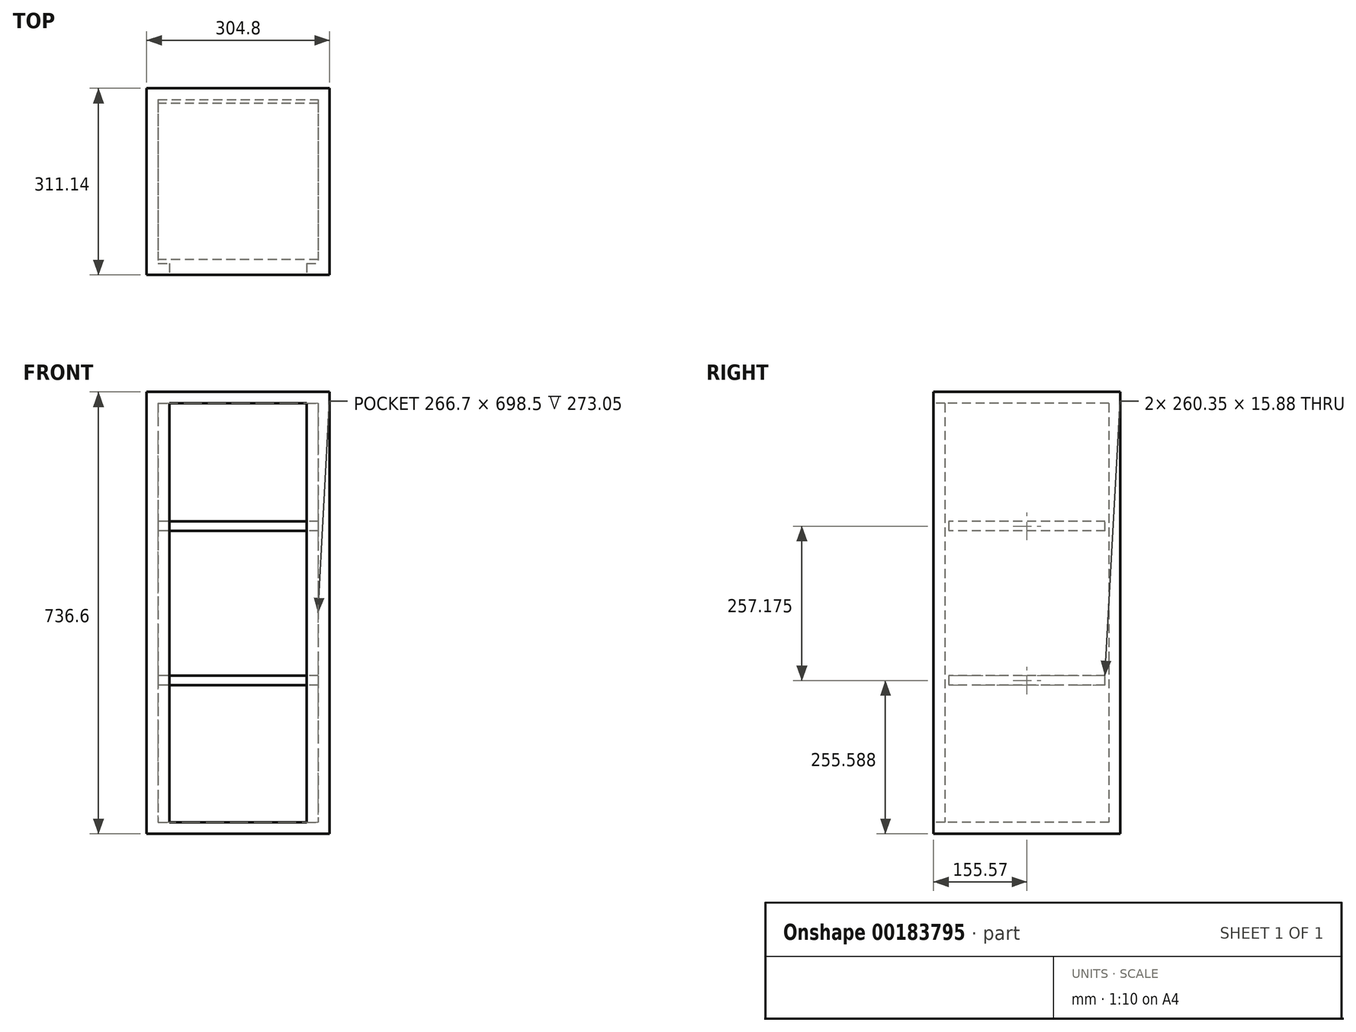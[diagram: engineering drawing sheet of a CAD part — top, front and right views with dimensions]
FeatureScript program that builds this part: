
annotation { "Feature Type Name" : "Feature", "Feature Type Description" : "" }
export const myFeature = defineFeature(function(context is Context, id is Id, definition is map)
    precondition{}
    {
        {
            var Q0;
            Q0=qCreatedBy(makeId("Top.planeOp"),FACE);
            var sketch = newSketch(context, id + "F0", { "sketchPlane" : qUnion([Q0])});
            skLineSegment(sketch, "E0.bottom", {"start": v(-133.35, 136.53) * mm, "end": v(133.35, 136.53) * mm});
            skLineSegment(sketch, "E0.top", {"start": v(-133.35, -136.53) * mm, "end": v(-114.3, -136.53) * mm});
            skLineSegment(sketch, "E0.left", {"start": v(-133.35, 136.52) * mm, "end": v(-133.35, -136.53) * mm});
            skLineSegment(sketch, "E0.right", {"start": v(133.35, 136.52) * mm, "end": v(133.35, -136.52) * mm});
            skLineSegment(sketch, "E1", {"start": v(133.35, 0) * mm, "end": v(-133.35, 0) * mm, "construction": true});
            skLineSegment(sketch, "E2", {"start": v(0, 136.53) * mm, "end": v(0, -136.53) * mm, "construction": true});
            skLineSegment(sketch, "E3.0", {"start": v(-152.4, 155.57) * mm, "end": v(152.4, 155.57) * mm});
            skLineSegment(sketch, "E3.1", {"start": v(-152.4, 155.57) * mm, "end": v(-152.4, -155.57) * mm});
            skLineSegment(sketch, "E3.2", {"start": v(-152.4, -155.57) * mm, "end": v(-114.3, -155.57) * mm});
            skLineSegment(sketch, "E3.3", {"start": v(152.4, 155.57) * mm, "end": v(152.4, -155.57) * mm});
            skLineSegment(sketch, "E4", {"start": v(114.3, -136.53) * mm, "end": v(114.3, -155.57) * mm});
            skLineSegment(sketch, "E5", {"start": v(-114.3, -136.53) * mm, "end": v(-114.3, -155.58) * mm});
            skLineSegment(sketch, "E6", {"start": v(-114.3, -136.53) * mm, "end": v(114.3, -136.53) * mm, "construction": true});
            skLineSegment(sketch, "E7", {"start": v(114.3, -136.53) * mm, "end": v(133.35, -136.53) * mm});
            skLineSegment(sketch, "E8", {"start": v(114.3, -155.57) * mm, "end": v(152.4, -155.57) * mm});
            skLineSegment(sketch, "E9", {"start": v(-114.3, -155.57) * mm, "end": v(114.3, -155.57) * mm, "construction": true});
            skSolve(sketch);
        }
        {
            var Q0;
            Q0=makeQuery(id+"F0.imprint","IMPRINT",FACE,{"disambiguationData":[TD([[makeQuery(id+"F0.imprint","IMPRINT",EDGE,{"derivedFrom":sQuery(id+"F0.wireOp",EDGE,"E0.bottom")}),1.0]])]});
            extrude(context, id + "F1", {"entities" : qUnion([Q0]), "depth" : 698.5 * mm});
        }
        {
            var Q0;
            Q0=makeQuery(id+"F1.opExtrude","CAP_FACE",FACE,{"disambiguationData":[OSD([sQuery(id+"F0.wireOp",EDGE,"E0.bottom"),sQuery(id+"F0.wireOp",EDGE,"E0.top"),sQuery(id+"F0.wireOp",EDGE,"E0.left"),sQuery(id+"F0.wireOp",EDGE,"E0.right"),sQuery(id+"F0.wireOp",EDGE,"E3.0"),sQuery(id+"F0.wireOp",EDGE,"E3.1"),sQuery(id+"F0.wireOp",EDGE,"E3.2"),sQuery(id+"F0.wireOp",EDGE,"E3.3"),sQuery(id+"F0.wireOp",EDGE,"E4"),sQuery(id+"F0.wireOp",EDGE,"E5"),sQuery(id+"F0.wireOp",EDGE,"E7"),sQuery(id+"F0.wireOp",EDGE,"E8")])],"isStart":false});
            var sketch = newSketch(context, id + "F2", { "sketchPlane" : qUnion([Q0])});
            skLineSegment(sketch, "E10.bottom", {"start": v(-152.4, 155.57) * mm, "end": v(152.4, 155.57) * mm});
            skLineSegment(sketch, "E10.top", {"start": v(-152.4, -155.57) * mm, "end": v(152.4, -155.57) * mm});
            skLineSegment(sketch, "E10.left", {"start": v(-152.4, 155.57) * mm, "end": v(-152.4, -155.57) * mm});
            skLineSegment(sketch, "E10.right", {"start": v(152.4, 155.57) * mm, "end": v(152.4, -155.57) * mm});
            skSolve(sketch);
        }
        {
            var Q0;
            Q0=makeQuery(id+"F2.imprint","IMPRINT",FACE,{"disambiguationData":[TD([[makeQuery(id+"F2.imprint","IMPRINT",EDGE,{"derivedFrom":sQuery(id+"F2.wireOp",EDGE,"E10.bottom")}),-1.0]])]});
            var Q1;
            Q1=makeQuery(id+"F2.imprint","IMPRINT",FACE,{"disambiguationData":[TD([[makeQuery(id+"F2.imprint","IMPRINT",EDGE,{"derivedFrom":makeQuery(id+"F1.opExtrude","CAP_EDGE",EDGE,{"disambiguationData":[OSD([sQuery(id+"F0.wireOp",EDGE,"E0.bottom")])],"isStart":false})}),-1.0]])]});
            extrude(context, id + "F3", {"entities" : qUnion([Q0, Q1]), "operationType" : NewBodyOperationType.ADD, "depth" : 19.05 * mm});
        }
        {
            var Q0;
            Q0=makeQuery(id+"F1.opExtrude","CAP_FACE",FACE,{"disambiguationData":[OSD([sQuery(id+"F0.wireOp",EDGE,"E0.bottom"),sQuery(id+"F0.wireOp",EDGE,"E0.top"),sQuery(id+"F0.wireOp",EDGE,"E0.left"),sQuery(id+"F0.wireOp",EDGE,"E0.right"),sQuery(id+"F0.wireOp",EDGE,"E3.0"),sQuery(id+"F0.wireOp",EDGE,"E3.1"),sQuery(id+"F0.wireOp",EDGE,"E3.2"),sQuery(id+"F0.wireOp",EDGE,"E3.3"),sQuery(id+"F0.wireOp",EDGE,"E4"),sQuery(id+"F0.wireOp",EDGE,"E5"),sQuery(id+"F0.wireOp",EDGE,"E7"),sQuery(id+"F0.wireOp",EDGE,"E8")])],"isStart":true});
            var sketch = newSketch(context, id + "F4", { "sketchPlane" : qUnion([Q0])});
            skLineSegment(sketch, "E11.bottom", {"start": v(-152.4, -155.57) * mm, "end": v(152.4, -155.57) * mm});
            skLineSegment(sketch, "E11.top", {"start": v(-152.4, 155.57) * mm, "end": v(152.4, 155.57) * mm});
            skLineSegment(sketch, "E11.left", {"start": v(-152.4, -155.57) * mm, "end": v(-152.4, 155.57) * mm});
            skLineSegment(sketch, "E11.right", {"start": v(152.4, -155.57) * mm, "end": v(152.4, 155.57) * mm});
            skSolve(sketch);
        }
        {
            var Q0;
            Q0=makeQuery(id+"F4.imprint","IMPRINT",FACE,{"disambiguationData":[TD([[makeQuery(id+"F4.imprint","IMPRINT",EDGE,{"derivedFrom":makeQuery(id+"F1.opExtrude","CAP_EDGE",EDGE,{"disambiguationData":[OSD([sQuery(id+"F0.wireOp",EDGE,"E0.bottom")])],"isStart":true})}),1.0]])]});
            var Q1;
            Q1=makeQuery(id+"F4.imprint","IMPRINT",FACE,{"disambiguationData":[TD([[makeQuery(id+"F4.imprint","IMPRINT",EDGE,{"derivedFrom":sQuery(id+"F4.wireOp",EDGE,"E11.bottom")}),1.0]])]});
            extrude(context, id + "F5", {"entities" : qUnion([Q0, Q1]), "operationType" : NewBodyOperationType.ADD, "depth" : 19.05 * mm});
        }
        {
            var Q0;
            Q0=makeQuery(id+"F1.opExtrude","SWEPT_FACE",FACE,{"disambiguationData":[OSD([sQuery(id+"F0.wireOp",EDGE,"E0.left")])]});
            var sketch = newSketch(context, id + "F6", { "sketchPlane" : qUnion([Q0])});
            skLineSegment(sketch, "E12.0", {"start": v(136.52, 228.6) * mm, "end": v(-136.53, 228.6) * mm});
            skLineSegment(sketch, "E13.0", {"start": v(136.52, 244.48) * mm, "end": v(-136.53, 244.48) * mm});
            skLineSegment(sketch, "E14.0", {"start": v(-130.18, 6.35) * mm, "end": v(130.17, 6.35) * mm});
            skLineSegment(sketch, "E14.1", {"start": v(-130.18, 692.15) * mm, "end": v(-130.18, 6.35) * mm});
            skLineSegment(sketch, "E14.2", {"start": v(130.17, 692.15) * mm, "end": v(-130.18, 692.15) * mm});
            skLineSegment(sketch, "E14.3", {"start": v(130.17, 6.35) * mm, "end": v(130.17, 692.15) * mm});
            skLineSegment(sketch, "E15.0", {"start": v(136.52, 485.78) * mm, "end": v(-136.53, 485.78) * mm});
            skLineSegment(sketch, "E16.0", {"start": v(136.52, 501.65) * mm, "end": v(-136.53, 501.65) * mm});
            skLineSegment(sketch, "E17", {"start": v(136.52, 501.65) * mm, "end": v(136.52, 485.78) * mm});
            skLineSegment(sketch, "E18", {"start": v(-136.53, 501.65) * mm, "end": v(-136.53, 485.78) * mm});
            skLineSegment(sketch, "E19", {"start": v(136.52, 244.48) * mm, "end": v(136.52, 228.6) * mm});
            skLineSegment(sketch, "E20", {"start": v(-136.53, 244.48) * mm, "end": v(-136.53, 228.6) * mm});
            skLineSegment(sketch, "E21.0", {"start": v(-155.58, 698.5) * mm, "end": v(-155.58, 0) * mm});
            skLineSegment(sketch, "E22.0", {"start": v(-136.53, 698.5) * mm, "end": v(-136.53, 0) * mm});
            skSolve(sketch);
        }
        {
            var Q0;
            {var subQ0=sQuery(id+"F6.wireOp",EDGE,"E14.3");var subQ1=sQuery(id+"F6.wireOp",EDGE,"E15.0");var subQ2=makeQuery(id+"F6.imprint","INTERSECT",VERTEX,{"derivedFrom":[subQ1,subQ0]});Q0=makeQuery(id+"F6.imprint","IMPRINT",FACE,{"disambiguationData":[TD([[makeQuery(id+"F6.imprint","IMPRINT",EDGE,{"disambiguationData":[TD([[subQ2,-1.0]])],"derivedFrom":subQ1}),-1.0]])]});}
            var Q1;
            {var subQ0=sQuery(id+"F6.wireOp",EDGE,"E14.3");var subQ1=sQuery(id+"F6.wireOp",EDGE,"E12.0");var subQ2=makeQuery(id+"F6.imprint","INTERSECT",VERTEX,{"derivedFrom":[subQ1,subQ0]});Q1=makeQuery(id+"F6.imprint","IMPRINT",FACE,{"disambiguationData":[TD([[makeQuery(id+"F6.imprint","IMPRINT",EDGE,{"disambiguationData":[TD([[subQ2,-1.0]])],"derivedFrom":subQ1}),-1.0]])]});}
            var Q2;
            Q2=makeQuery(id+"F1.opExtrude","SWEPT_FACE",FACE,{"disambiguationData":[OSD([sQuery(id+"F0.wireOp",EDGE,"E0.right")])]});
            extrude(context, id + "F7", {"entities" : qUnion([Q0, Q1]), "operationType" : NewBodyOperationType.ADD, "endBound" : BoundingType.UP_TO_SURFACE, "endBoundEntityFace" : qUnion([Q2]), "depth" : 25.4 * mm});
        }
    });
